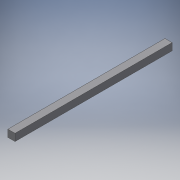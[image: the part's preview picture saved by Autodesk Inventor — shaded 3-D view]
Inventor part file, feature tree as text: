
AUTODESK INVENTOR PART (.ipt)
format: ipt  version: 2018 (Build 220112000, 112)  size: 92,672 bytes
history: native  units: in
note: dims shown in document units (in); Inventor stores cm internally (conversion verified against a paired STEP export)
features: extrude x1, sketch x1
ambient origin geometry x8: Origin, YZ Plane, XZ Plane, XY Plane, X Axis, Y Axis, Z Axis, Center Point
bodies: Solid1 (feature_tree)
feature tree (2):
  extrude  "Extrusion1"  Depth=22.0in
  sketch  "Sketch1"  dims[d0=1.0in d1=22.0in d2=1.0in d3=0.0in]
